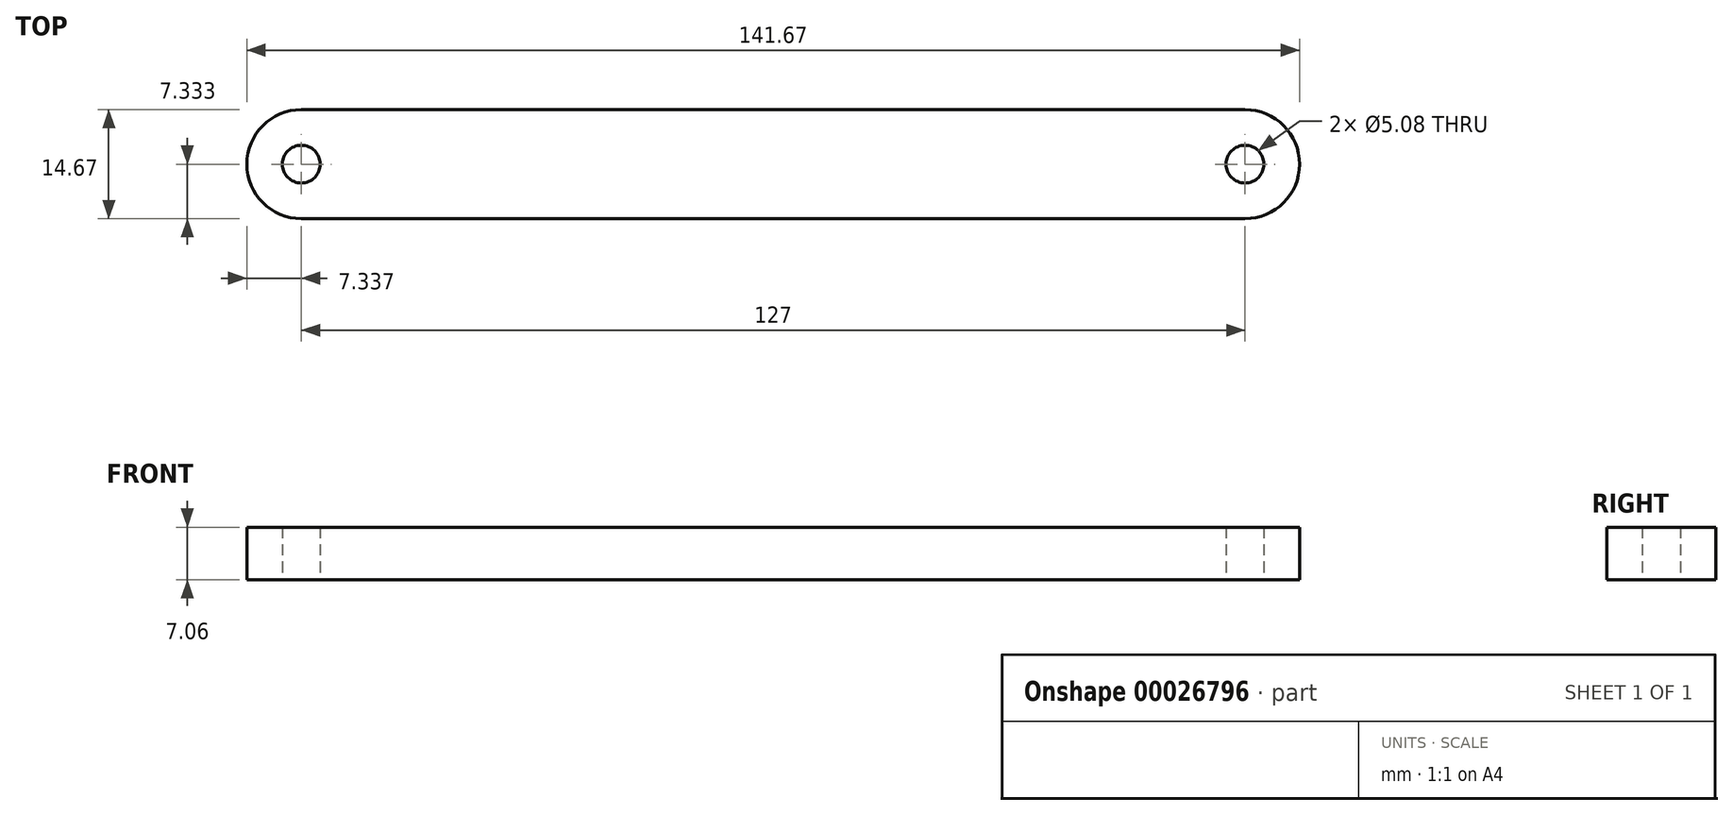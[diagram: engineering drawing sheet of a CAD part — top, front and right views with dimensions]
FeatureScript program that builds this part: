
annotation { "Feature Type Name" : "Feature", "Feature Type Description" : "" }
export const myFeature = defineFeature(function(context is Context, id is Id, definition is map)
    precondition{}
    {
        {
            var Q0;
            Q0=qCreatedBy(makeId("Top.planeOp"),FACE);
            var sketch = newSketch(context, id + "F0", { "sketchPlane" : qUnion([Q0])});
            skLineSegment(sketch, "E0.bottom", {"start": v(-34.23, 17.32) * mm, "end": v(92.77, 17.32) * mm});
            skLineSegment(sketch, "E0.top", {"start": v(-34.23, 2.65) * mm, "end": v(92.77, 2.65) * mm});
            skArc(sketch, "E1", {"start": v(-34.23, 17.32) * mm, "mid": v(-41.57, 9.98) * mm, "end": v(-34.23, 2.65) * mm});
            skArc(sketch, "E2", {"start": v(92.77, 2.65) * mm, "mid": v(100.1, 9.98) * mm, "end": v(92.77, 17.32) * mm});
            skCircle(sketch, "E3", {"center": v(-34.23, 9.98) * mm, "radius": 2.54 * mm});
            skCircle(sketch, "E4", {"center": v(92.77, 9.98) * mm, "radius": 2.54 * mm});
            skLineSegment(sketch, "E5", {"start": v(22.68, 2.65) * mm, "end": v(22.68, 17.32) * mm});
            skSolve(sketch);
        }
        {
            var Q0;
            Q0 = qSketchRegion(id + "F0", true);
            extrude(context, id + "F1", {"entities" : qUnion([Q0]), "depth" : 7.06 * mm});
        }
    });
